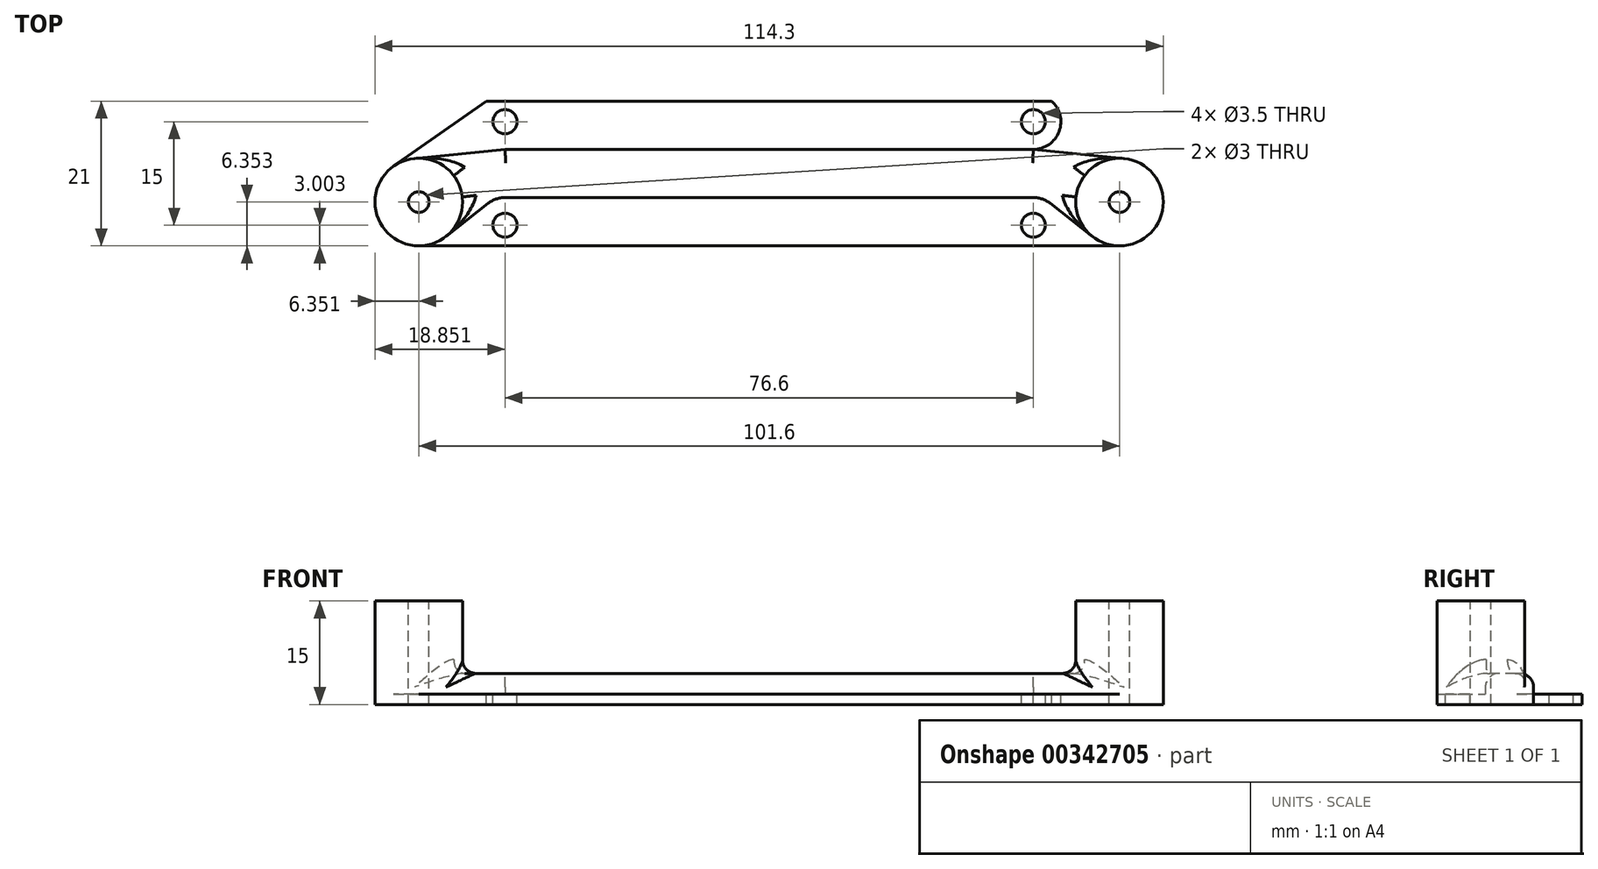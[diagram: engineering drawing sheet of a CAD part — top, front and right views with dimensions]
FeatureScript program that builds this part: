
annotation { "Feature Type Name" : "Feature", "Feature Type Description" : "" }
export const myFeature = defineFeature(function(context is Context, id is Id, definition is map)
    precondition{}
    {
        {
            var Q0;
            Q0=qCreatedBy(makeId("Top.planeOp"),FACE);
            var sketch = newSketch(context, id + "F0", { "sketchPlane" : qUnion([Q0])});
            skLineSegment(sketch, "E0", {"start": v(-53.06, 9.45) * mm, "end": v(-53.06, -10.66) * mm, "construction": true});
            skLineSegment(sketch, "E1", {"start": v(48.54, 9.45) * mm, "end": v(48.54, -11.55) * mm, "construction": true});
            skLineSegment(sketch, "E2", {"start": v(-63.06, -11.55) * mm, "end": v(83.55, -11.55) * mm});
            skLineSegment(sketch, "E3", {"start": v(-63.06, -5.2) * mm, "end": v(83.55, -5.2) * mm, "construction": true});
            skCircle(sketch, "E4", {"center": v(-53.06, -5.2) * mm, "radius": 1.5 * mm});
            skLineSegment(sketch, "E5", {"start": v(-63.06, 9.45) * mm, "end": v(-63.06, -11.55) * mm, "construction": true});
            skCircle(sketch, "E6", {"center": v(48.54, -5.2) * mm, "radius": 1.5 * mm});
            skLineSegment(sketch, "E7", {"start": v(-63.06, 9.45) * mm, "end": v(83.55, 9.45) * mm, "construction": true});
            skLineSegment(sketch, "E8", {"start": v(-40.56, 29.45) * mm, "end": v(-40.56, -16.55) * mm, "construction": true});
            skLineSegment(sketch, "E9", {"start": v(36.04, 9.45) * mm, "end": v(36.04, -11.55) * mm, "construction": true});
            skLineSegment(sketch, "E10", {"start": v(-63.06, 9.45) * mm, "end": v(83.55, 9.45) * mm});
            skLineSegment(sketch, "E11", {"start": v(58.54, 9.45) * mm, "end": v(58.15, -34.37) * mm, "construction": true});
            skLineSegment(sketch, "E12", {"start": v(58.54, 9.45) * mm, "end": v(-63.06, 9.45) * mm});
            skLineSegment(sketch, "E13", {"start": v(-63.06, 9.45) * mm, "end": v(-63.06, -11.55) * mm});
            skLineSegment(sketch, "E14", {"start": v(58.54, 9.45) * mm, "end": v(58.54, -11.55) * mm});
            skLineSegment(sketch, "E15", {"start": v(-40.56, -8.55) * mm, "end": v(36.04, -8.55) * mm, "construction": true});
            skLineSegment(sketch, "E16", {"start": v(-40.56, 6.45) * mm, "end": v(36.04, 6.45) * mm, "construction": true});
            skCircle(sketch, "E17", {"center": v(-40.56, -8.55) * mm, "radius": 1.75 * mm});
            skCircle(sketch, "E18", {"center": v(-40.56, 6.45) * mm, "radius": 1.75 * mm});
            skCircle(sketch, "E19", {"center": v(36.04, 6.45) * mm, "radius": 1.75 * mm});
            skCircle(sketch, "E20", {"center": v(36.04, -8.55) * mm, "radius": 1.75 * mm});
            skCircle(sketch, "E21", {"center": v(-53.06, -5.2) * mm, "radius": 6.35 * mm});
            skCircle(sketch, "E22", {"center": v(48.54, -5.2) * mm, "radius": 6.35 * mm});
            skCircle(sketch, "E23", {"center": v(-40.56, -8.55) * mm, "radius": 4 * mm});
            skCircle(sketch, "E24", {"center": v(-40.56, 6.45) * mm, "radius": 4 * mm});
            skLineSegment(sketch, "E25", {"start": v(-40.56, 2.45) * mm, "end": v(-53.7, 1.12) * mm});
            skCircle(sketch, "E26", {"center": v(36.04, 6.45) * mm, "radius": 4 * mm});
            skCircle(sketch, "E27", {"center": v(36.04, -8.55) * mm, "radius": 4 * mm});
            skLineSegment(sketch, "E28", {"start": v(-40.56, -4.55) * mm, "end": v(36.04, -4.55) * mm});
            skLineSegment(sketch, "E29", {"start": v(36.04, 2.45) * mm, "end": v(-40.56, 2.45) * mm});
            skPoint(sketch, "E29.startSnap0", {"position": v(36.04, -1.05) * mm});
            skLineSegment(sketch, "E30", {"start": v(44.62, -10.2) * mm, "end": v(36.04, -3.46) * mm});
            skLineSegment(sketch, "E31", {"start": v(-56.7, 0) * mm, "end": v(-43.25, 9.45) * mm});
            skLineSegment(sketch, "E32", {"start": v(-43.25, 9.45) * mm, "end": v(-43.27, 9.83) * mm});
            skLineSegment(sketch, "E33", {"start": v(38.34, 9.73) * mm, "end": v(55.17, -2.09) * mm});
            skLineSegment(sketch, "E34", {"start": v(36.04, 2.45) * mm, "end": v(50.83, 0.95) * mm});
            skLineSegment(sketch, "E35", {"start": v(-49.14, -10.2) * mm, "end": v(-43.03, -5.4) * mm});
            skSolve(sketch);
        }
        {
            var Q0;
            {var subQ10=sQuery(id+"F0.wireOp",EDGE,"E25");Q0=makeQuery(id+"F0.imprint","IMPRINT",FACE,{"disambiguationData":[TD([[makeQuery(id+"F0.imprint","IMPRINT",EDGE,{"derivedFrom":subQ10}),1.0]])]});}
            var Q1;
            {var subQ4=sQuery(id+"F0.wireOp",EDGE,"E33");var subQ6=sQuery(id+"F0.wireOp",EDGE,"E12");var subQ7=makeQuery(id+"F0.imprint","INTERSECT",VERTEX,{"derivedFrom":[subQ6,subQ4]});Q1=makeQuery(id+"F0.imprint","IMPRINT",FACE,{"disambiguationData":[TD([[makeQuery(id+"F0.imprint","IMPRINT",EDGE,{"disambiguationData":[TD([[subQ7,-1.0]])],"derivedFrom":subQ6}),1.0]])]});}
            var Q2;
            Q2=makeQuery(id+"F0.imprint","IMPRINT",FACE,{"disambiguationData":[TD([[makeQuery(id+"F0.imprint","IMPRINT",EDGE,{"derivedFrom":sQuery(id+"F0.wireOp",EDGE,"E19")}),-1.0]])]});
            var Q3;
            {var subQ5=sQuery(id+"F0.wireOp",EDGE,"E29");Q3=makeQuery(id+"F0.imprint","IMPRINT",FACE,{"disambiguationData":[TD([[makeQuery(id+"F0.imprint","IMPRINT",EDGE,{"derivedFrom":subQ5}),-1.0]])]});}
            var Q4;
            Q4=makeQuery(id+"F0.imprint","IMPRINT",FACE,{"disambiguationData":[TD([[makeQuery(id+"F0.imprint","IMPRINT",EDGE,{"derivedFrom":sQuery(id+"F0.wireOp",EDGE,"E6")}),-1.0]])]});
            var Q5;
            {var subQ0=sQuery(id+"F0.wireOp",EDGE,"E27");var subQ1=sQuery(id+"F0.wireOp",EDGE,"E2");var subQ2=makeQuery(id+"F0.imprint","INTERSECT",VERTEX,{"disambiguationData":[OD(1.0)],"derivedFrom":[subQ1,subQ0]});Q5=makeQuery(id+"F0.imprint","IMPRINT",FACE,{"disambiguationData":[TD([[makeQuery(id+"F0.imprint","IMPRINT",EDGE,{"disambiguationData":[TD([[subQ2,-1.0]])],"derivedFrom":subQ1}),1.0]])]});}
            var Q6;
            Q6=makeQuery(id+"F0.imprint","IMPRINT",FACE,{"disambiguationData":[TD([[makeQuery(id+"F0.imprint","IMPRINT",EDGE,{"derivedFrom":sQuery(id+"F0.wireOp",EDGE,"E20")}),-1.0]])]});
            var Q7;
            {var subQ5=sQuery(id+"F0.wireOp",EDGE,"E28");Q7=makeQuery(id+"F0.imprint","IMPRINT",FACE,{"disambiguationData":[TD([[makeQuery(id+"F0.imprint","IMPRINT",EDGE,{"derivedFrom":subQ5}),-1.0]])]});}
            var Q8;
            Q8=makeQuery(id+"F0.imprint","IMPRINT",FACE,{"disambiguationData":[TD([[makeQuery(id+"F0.imprint","IMPRINT",EDGE,{"derivedFrom":sQuery(id+"F0.wireOp",EDGE,"E17")}),-1.0]])]});
            var Q9;
            Q9=makeQuery(id+"F0.imprint","IMPRINT",FACE,{"disambiguationData":[TD([[makeQuery(id+"F0.imprint","IMPRINT",EDGE,{"derivedFrom":sQuery(id+"F0.wireOp",EDGE,"E4")}),-1.0]])]});
            var Q10;
            {var subQ0=sQuery(id+"F0.wireOp",EDGE,"E25");Q10=makeQuery(id+"F0.imprint","IMPRINT",FACE,{"disambiguationData":[TD([[makeQuery(id+"F0.imprint","IMPRINT",EDGE,{"derivedFrom":subQ0}),-1.0]])]});}
            var Q11;
            Q11=makeQuery(id+"F0.imprint","IMPRINT",FACE,{"disambiguationData":[TD([[makeQuery(id+"F0.imprint","IMPRINT",EDGE,{"derivedFrom":sQuery(id+"F0.wireOp",EDGE,"E18")}),-1.0]])]});
            var Q12;
            {var subQ5=sQuery(id+"F0.wireOp",EDGE,"E35");Q12=makeQuery(id+"F0.imprint","IMPRINT",FACE,{"disambiguationData":[TD([[makeQuery(id+"F0.imprint","IMPRINT",EDGE,{"derivedFrom":subQ5}),-1.0]])]});}
            extrude(context, id + "F1", {"entities" : qUnion([Q0, Q1, Q2, Q3, Q4, Q5, Q6, Q7, Q8, Q9, Q10, Q11, Q12]), "oppositeDirection" : true, "depth" : 1.5 * mm});
        }
        {
            var Q0;
            {var subQ0=sQuery(id+"F0.wireOp",EDGE,"E25");Q0=makeQuery(id+"F0.imprint","IMPRINT",FACE,{"disambiguationData":[TD([[makeQuery(id+"F0.imprint","IMPRINT",EDGE,{"derivedFrom":subQ0}),1.0]])]});}
            extrude(context, id + "F2", {"entities" : qUnion([Q0]), "operationType" : NewBodyOperationType.ADD, "depth" : 3 * mm});
        }
        {
            var Q0;
            Q0=makeQuery(id+"F0.imprint","IMPRINT",FACE,{"disambiguationData":[TD([[makeQuery(id+"F0.imprint","IMPRINT",EDGE,{"derivedFrom":sQuery(id+"F0.wireOp",EDGE,"E6")}),-1.0]])]});
            var Q1;
            Q1=makeQuery(id+"F0.imprint","IMPRINT",FACE,{"disambiguationData":[TD([[makeQuery(id+"F0.imprint","IMPRINT",EDGE,{"derivedFrom":sQuery(id+"F0.wireOp",EDGE,"E4")}),-1.0]])]});
            extrude(context, id + "F3", {"entities" : qUnion([Q0, Q1]), "operationType" : NewBodyOperationType.ADD, "depth" : 13.5 * mm});
        }
        {
            var Q0;
            Q0=makeQuery(id+"F2.opExtrude","CAP_EDGE",EDGE,{"disambiguationData":[OSD([sQuery(id+"F0.wireOp",EDGE,"E29")])],"isStart":false});
            var Q1;
            Q1=makeQuery(id+"F2.opExtrude","CAP_EDGE",EDGE,{"disambiguationData":[OSD([sQuery(id+"F0.wireOp",EDGE,"E28")])],"isStart":false});
            var Q2;
            Q2=makeQuery(id+"F2.opExtrude","CAP_FACE",FACE,{"disambiguationData":[OSD([sQuery(id+"F0.wireOp",EDGE,"E21"),sQuery(id+"F0.wireOp",EDGE,"E22"),sQuery(id+"F0.wireOp",EDGE,"E23"),sQuery(id+"F0.wireOp",EDGE,"E25"),sQuery(id+"F0.wireOp",EDGE,"E27"),sQuery(id+"F0.wireOp",EDGE,"E28"),sQuery(id+"F0.wireOp",EDGE,"E29"),sQuery(id+"F0.wireOp",EDGE,"E30"),sQuery(id+"F0.wireOp",EDGE,"E34"),sQuery(id+"F0.wireOp",EDGE,"E35")])],"isStart":false});
            fillet(context, id + "F4", {"entities" : qUnion([Q0, Q1, Q2]), "radius" : 2 * mm, "tangentPropagation" : true, "allowEdgeOverflow" : false});
        }
    });
